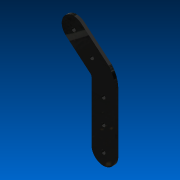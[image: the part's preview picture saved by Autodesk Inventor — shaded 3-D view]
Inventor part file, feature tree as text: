
AUTODESK INVENTOR PART (.ipt)
format: ipt  version: 2022 (Build 260153000, 153)  size: 115,712 bytes
history: native  units: in
note: dims shown in document units (in); Inventor stores cm internally (conversion verified against a paired STEP export)
features: sketch x1, extrude x1, hole x1
ambient origin geometry x8: Origin, YZ Plane, XZ Plane, XY Plane, X Axis, Y Axis, Z Axis, Center Point
bodies: Solid1 (feature_tree)
feature tree (3):
  sketch  "Sketch1"  dims[d0=1.0in d1=2.0in d2=1.0in d3=0.5in d4=0.125in d5=0.0in d7=0.175in d8=0.75in d9=0.375in d10=0.25in d11=0.5635in d12=1.0in d13=0.8108in d14=1.0in]
  extrude  "Extrusion1"  Depth=1.0in
  hole  "Hole1"  [1 undecoded]
note: 1 required parameter value undecoded (feature->parameter linkage not recoverable at this tier; creation-order binding heuristic only, values carry confidence <= 0.55)
